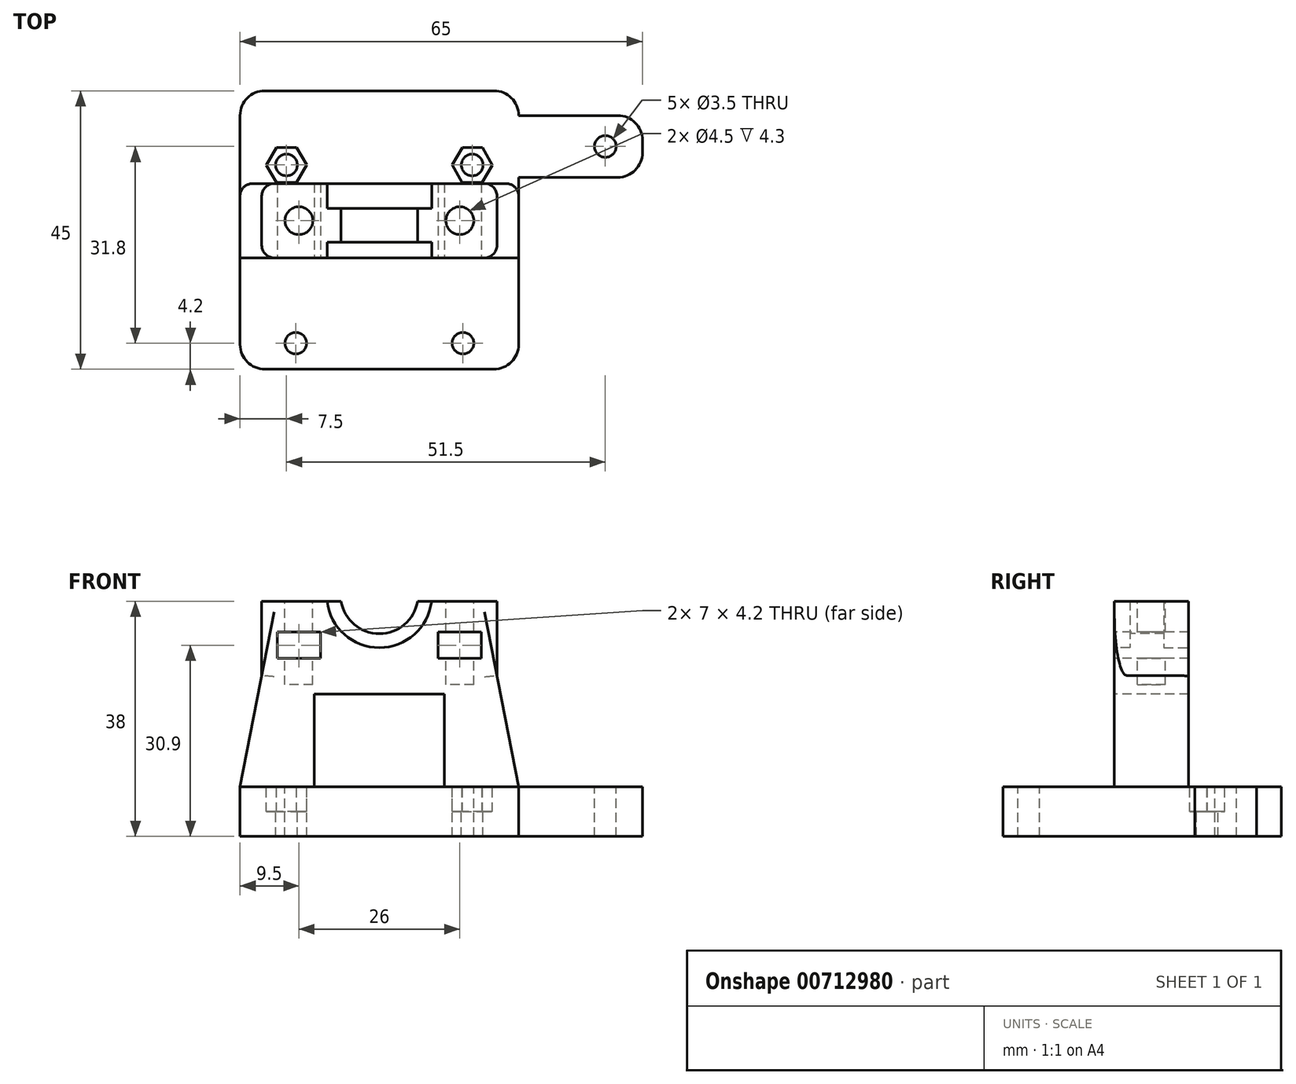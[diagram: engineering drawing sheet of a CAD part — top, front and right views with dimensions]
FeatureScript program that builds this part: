
annotation { "Feature Type Name" : "Feature", "Feature Type Description" : "" }
export const myFeature = defineFeature(function(context is Context, id is Id, definition is map)
    precondition{}
    {
        {
            var Q0;
            Q0=qCreatedBy(makeId("Top.planeOp"),FACE);
            var sketch = newSketch(context, id + "F0", { "sketchPlane" : qUnion([Q0])});
            skLineSegment(sketch, "E0.bottom", {"start": v(22.5, 22.5) * mm, "end": v(-22.5, 22.5) * mm});
            skLineSegment(sketch, "E0.top", {"start": v(22.5, -22.5) * mm, "end": v(-22.5, -22.5) * mm});
            skLineSegment(sketch, "E0.left", {"start": v(22.5, 22.5) * mm, "end": v(22.5, -22.5) * mm});
            skLineSegment(sketch, "E0.right", {"start": v(-22.5, 22.5) * mm, "end": v(-22.5, -22.5) * mm});
            skPoint(sketch, "E0.middle", {"position": v(0, 0) * mm});
            skLineSegment(sketch, "E1.bottom", {"start": v(22.5, 8.5) * mm, "end": v(42.5, 8.5) * mm});
            skLineSegment(sketch, "E1.top", {"start": v(22.5, 18.5) * mm, "end": v(42.5, 18.5) * mm});
            skLineSegment(sketch, "E1.left", {"start": v(22.5, 8.5) * mm, "end": v(22.5, 18.5) * mm});
            skLineSegment(sketch, "E1.right", {"start": v(42.5, 8.5) * mm, "end": v(42.5, 18.5) * mm});
            skSolve(sketch);
        }
        {
            var Q0;
            {var subQ3=sQuery(id+"F0.wireOp",EDGE,"E0.bottom");Q0=makeQuery(id+"F0.imprint","IMPRINT",FACE,{"disambiguationData":[TD([[makeQuery(id+"F0.imprint","IMPRINT",EDGE,{"derivedFrom":subQ3}),1.0]])]});}
            var Q1;
            Q1=makeQuery(id+"F0.imprint","IMPRINT",FACE,{"disambiguationData":[TD([[makeQuery(id+"F0.imprint","IMPRINT",EDGE,{"derivedFrom":sQuery(id+"F0.wireOp",EDGE,"E1.bottom")}),1.0]])]});
            extrude(context, id + "F1", {"entities" : qUnion([Q0, Q1]), "depth" : 8 * mm, "offsetDistance" : 25 * mm});
        }
        {
            var Q0;
            Q0=makeQuery(id+"F1.opExtrude","CAP_FACE",FACE,{"disambiguationData":[OSD([sQuery(id+"F0.wireOp",EDGE,"E0.bottom"),sQuery(id+"F0.wireOp",EDGE,"E0.top"),sQuery(id+"F0.wireOp",EDGE,"E0.left"),sQuery(id+"F0.wireOp",EDGE,"E0.right"),sQuery(id+"F0.wireOp",EDGE,"E1.bottom"),sQuery(id+"F0.wireOp",EDGE,"E1.top"),sQuery(id+"F0.wireOp",EDGE,"E1.right")])],"isStart":false});
            var sketch = newSketch(context, id + "F2", { "sketchPlane" : qUnion([Q0])});
            skLineSegment(sketch, "E2.bottom", {"start": v(-22.5, -4.5) * mm, "end": v(22.5, -4.5) * mm});
            skLineSegment(sketch, "E2.top", {"start": v(-22.5, 7.5) * mm, "end": v(22.5, 7.5) * mm});
            skLineSegment(sketch, "E2.left", {"start": v(-22.5, -4.5) * mm, "end": v(-22.5, 7.5) * mm});
            skLineSegment(sketch, "E2.right", {"start": v(22.5, -4.5) * mm, "end": v(22.5, 7.5) * mm});
            skSolve(sketch);
        }
        {
            var Q0;
            Q0=makeQuery(id+"F2.imprint","IMPRINT",FACE,{"disambiguationData":[TD([[makeQuery(id+"F2.imprint","IMPRINT",EDGE,{"derivedFrom":sQuery(id+"F2.wireOp",EDGE,"E2.bottom")}),1.0]])]});
            extrude(context, id + "F3", {"entities" : qUnion([Q0]), "operationType" : NewBodyOperationType.ADD, "depth" : 18 * mm, "offsetDistance" : 25 * mm});
        }
        {
            var Q0;
            Q0=makeQuery(id+"F3.opExtrude","CAP_FACE",FACE,{"disambiguationData":[OSD([sQuery(id+"F2.wireOp",EDGE,"E2.bottom"),sQuery(id+"F2.wireOp",EDGE,"E2.top"),sQuery(id+"F2.wireOp",EDGE,"E2.left"),sQuery(id+"F2.wireOp",EDGE,"E2.right")])],"isStart":false});
            var sketch = newSketch(context, id + "F4", { "sketchPlane" : qUnion([Q0])});
            skLineSegment(sketch, "E3.bottom", {"start": v(-19, 7.5) * mm, "end": v(19, 7.5) * mm});
            skLineSegment(sketch, "E3.top", {"start": v(-19, -4.5) * mm, "end": v(19, -4.5) * mm});
            skLineSegment(sketch, "E3.left", {"start": v(-19, 7.5) * mm, "end": v(-19, -4.5) * mm});
            skLineSegment(sketch, "E3.right", {"start": v(19, 7.5) * mm, "end": v(19, -4.5) * mm});
            skSolve(sketch);
        }
        {
            var Q0;
            Q0=makeQuery(id+"F4.imprint","IMPRINT",FACE,{"disambiguationData":[TD([[makeQuery(id+"F4.imprint","IMPRINT",EDGE,{"derivedFrom":sQuery(id+"F4.wireOp",EDGE,"E3.bottom")}),-1.0]])]});
            extrude(context, id + "F5", {"entities" : qUnion([Q0]), "operationType" : NewBodyOperationType.ADD, "depth" : 12 * mm, "offsetDistance" : 25 * mm});
        }
        {
            var Q0;
            Q0=makeQuery(id+"F5.boolean.opBoolean","MERGE",FACE,{"derivedFrom":[makeQuery(id+"F3.opExtrude","SWEPT_FACE",FACE,{"disambiguationData":[OSD([sQuery(id+"F2.wireOp",EDGE,"E2.bottom")])]}),makeQuery(id+"F5.opExtrude","SWEPT_FACE",FACE,{"disambiguationData":[OSD([sQuery(id+"F4.wireOp",EDGE,"E3.top")])]})]});
            var sketch = newSketch(context, id + "F6", { "sketchPlane" : qUnion([Q0])});
            skLineSegment(sketch, "E4", {"start": v(-19, 26) * mm, "end": v(-22.5, 8) * mm});
            skLineSegment(sketch, "E5", {"start": v(-22.5, 8) * mm, "end": v(-22.5, 26) * mm});
            skLineSegment(sketch, "E6", {"start": v(-22.5, 26) * mm, "end": v(-19, 26) * mm});
            skLineSegment(sketch, "E7", {"start": v(19, 26) * mm, "end": v(22.5, 26) * mm});
            skLineSegment(sketch, "E8", {"start": v(22.5, 26) * mm, "end": v(22.5, 8) * mm});
            skLineSegment(sketch, "E9", {"start": v(22.5, 8) * mm, "end": v(19, 26) * mm});
            skSolve(sketch);
        }
        {
            var Q0;
            Q0=makeQuery(id+"F6.imprint","IMPRINT",FACE,{"disambiguationData":[TD([[makeQuery(id+"F6.imprint","IMPRINT",EDGE,{"derivedFrom":sQuery(id+"F6.wireOp",EDGE,"E4")}),-1.0]])]});
            var Q1;
            Q1=makeQuery(id+"F6.imprint","IMPRINT",FACE,{"disambiguationData":[TD([[makeQuery(id+"F6.imprint","IMPRINT",EDGE,{"derivedFrom":sQuery(id+"F6.wireOp",EDGE,"E7")}),-1.0]])]});
            extrude(context, id + "F7", {"entities" : qUnion([Q0, Q1]), "operationType" : NewBodyOperationType.REMOVE, "oppositeDirection" : true, "depth" : 25 * mm, "offsetDistance" : 25 * mm});
        }
        {
            var Q0;
            Q0=makeQuery(id+"F5.boolean.opBoolean","MERGE",FACE,{"derivedFrom":[makeQuery(id+"F3.opExtrude","SWEPT_FACE",FACE,{"disambiguationData":[OSD([sQuery(id+"F2.wireOp",EDGE,"E2.bottom")])]}),makeQuery(id+"F5.opExtrude","SWEPT_FACE",FACE,{"disambiguationData":[OSD([sQuery(id+"F4.wireOp",EDGE,"E3.top")])]})]});
            var sketch = newSketch(context, id + "F8", { "sketchPlane" : qUnion([Q0])});
            skLineSegment(sketch, "E10.bottom", {"start": v(-10.5, 8) * mm, "end": v(10.5, 8) * mm});
            skLineSegment(sketch, "E10.top", {"start": v(-10.5, 23) * mm, "end": v(10.5, 23) * mm});
            skLineSegment(sketch, "E10.left", {"start": v(-10.5, 8) * mm, "end": v(-10.5, 23) * mm});
            skLineSegment(sketch, "E10.right", {"start": v(10.5, 8) * mm, "end": v(10.5, 23) * mm});
            skSolve(sketch);
        }
        {
            var Q0;
            Q0=makeQuery(id+"F8.imprint","IMPRINT",FACE,{"disambiguationData":[TD([[makeQuery(id+"F8.imprint","IMPRINT",EDGE,{"derivedFrom":sQuery(id+"F8.wireOp",EDGE,"E10.bottom")}),1.0]])]});
            extrude(context, id + "F9", {"entities" : qUnion([Q0]), "operationType" : NewBodyOperationType.REMOVE, "oppositeDirection" : true, "depth" : 25 * mm, "offsetDistance" : 25 * mm});
        }
        {
            var Q0;
            {var subQ0=sQuery(id+"F0.wireOp",EDGE,"E0.right");var subQ3=sQuery(id+"F0.wireOp",EDGE,"E0.left");var subQ4=sQuery(id+"F0.wireOp",EDGE,"E0.bottom");var subQ6=sQuery(id+"F0.wireOp",EDGE,"E1.top");var subQ7=sQuery(id+"F0.wireOp",EDGE,"E0.top");var subQ8=sQuery(id+"F0.wireOp",EDGE,"E1.bottom");var subQ11=sQuery(id+"F0.wireOp",EDGE,"E1.right");var subQ12=makeQuery(id+"F1.opExtrude","CAP_FACE",FACE,{"disambiguationData":[OSD([subQ4,subQ7,subQ3,subQ0,subQ8,subQ6,subQ11])],"isStart":false});Q0=makeQuery(id+"F9.boolean.opBoolean","MERGE",FACE,{"derivedFrom":[makeQuery(id+"F3.boolean.opBoolean","SPLIT",FACE,{"disambiguationData":[TD([makeQuery(id+"F1.opExtrude","SWEPT_FACE",FACE,{"disambiguationData":[OSD([subQ7])]})])],"derivedFrom":subQ12}),makeQuery(id+"F3.boolean.opBoolean","SPLIT",FACE,{"disambiguationData":[TD([makeQuery(id+"F1.opExtrude","SWEPT_FACE",FACE,{"disambiguationData":[OSD([subQ4])]})])],"derivedFrom":subQ12}),makeQuery(id+"F9.opExtrude","SWEPT_FACE",FACE,{"disambiguationData":[OSD([sQuery(id+"F8.wireOp",EDGE,"E10.bottom")])]})]});}
            var sketch = newSketch(context, id + "F10", { "sketchPlane" : qUnion([Q0])});
            skCircle(sketch, "E11", {"center": v(-15, 10.5) * mm, "radius": 1.75 * mm});
            skLineSegment(sketch, "E12", {"start": v(-15, 10.5) * mm, "end": v(15, 10.5) * mm, "construction": true});
            skCircle(sketch, "E13", {"center": v(15, 10.5) * mm, "radius": 1.75 * mm});
            skSolve(sketch);
        }
        {
            var Q0;
            Q0=makeQuery(id+"F10.imprint","IMPRINT",FACE,{"disambiguationData":[TD([[makeQuery(id+"F10.imprint","IMPRINT",EDGE,{"derivedFrom":sQuery(id+"F10.wireOp",EDGE,"E11")}),1.0]])]});
            var Q1;
            Q1=makeQuery(id+"F10.imprint","IMPRINT",FACE,{"disambiguationData":[TD([[makeQuery(id+"F10.imprint","IMPRINT",EDGE,{"derivedFrom":sQuery(id+"F10.wireOp",EDGE,"E13")}),1.0]])]});
            extrude(context, id + "F11", {"entities" : qUnion([Q0, Q1]), "operationType" : NewBodyOperationType.REMOVE, "oppositeDirection" : true, "depth" : 25 * mm, "offsetDistance" : 25 * mm});
        }
        {
            var Q0;
            {var subQ0=sQuery(id+"F0.wireOp",EDGE,"E0.right");var subQ3=sQuery(id+"F0.wireOp",EDGE,"E0.left");var subQ4=sQuery(id+"F0.wireOp",EDGE,"E0.bottom");var subQ6=sQuery(id+"F0.wireOp",EDGE,"E1.top");var subQ7=sQuery(id+"F0.wireOp",EDGE,"E0.top");var subQ8=sQuery(id+"F0.wireOp",EDGE,"E1.bottom");var subQ11=sQuery(id+"F0.wireOp",EDGE,"E1.right");var subQ12=makeQuery(id+"F1.opExtrude","CAP_FACE",FACE,{"disambiguationData":[OSD([subQ4,subQ7,subQ3,subQ0,subQ8,subQ6,subQ11])],"isStart":false});Q0=makeQuery(id+"F9.boolean.opBoolean","MERGE",FACE,{"derivedFrom":[makeQuery(id+"F3.boolean.opBoolean","SPLIT",FACE,{"disambiguationData":[TD([makeQuery(id+"F1.opExtrude","SWEPT_FACE",FACE,{"disambiguationData":[OSD([subQ7])]})])],"derivedFrom":subQ12}),makeQuery(id+"F3.boolean.opBoolean","SPLIT",FACE,{"disambiguationData":[TD([makeQuery(id+"F1.opExtrude","SWEPT_FACE",FACE,{"disambiguationData":[OSD([subQ4])]})])],"derivedFrom":subQ12}),makeQuery(id+"F9.opExtrude","SWEPT_FACE",FACE,{"disambiguationData":[OSD([sQuery(id+"F8.wireOp",EDGE,"E10.bottom")])]})]});}
            var sketch = newSketch(context, id + "F12", { "sketchPlane" : qUnion([Q0])});
            skCircle(sketch, "E14.cCircle", {"center": v(-15, 10.5) * mm, "radius": 3.25 * mm, "construction": true});
            skLineSegment(sketch, "E14.0", {"start": v(-13.4, 13.32) * mm, "end": v(-11.75, 10.52) * mm});
            skLineSegment(sketch, "E14.1", {"start": v(-11.75, 10.52) * mm, "end": v(-13.36, 7.7) * mm});
            skLineSegment(sketch, "E14.2", {"start": v(-13.36, 7.7) * mm, "end": v(-16.6, 7.68) * mm});
            skLineSegment(sketch, "E14.3", {"start": v(-16.6, 7.68) * mm, "end": v(-18.25, 10.48) * mm});
            skLineSegment(sketch, "E14.4", {"start": v(-18.25, 10.48) * mm, "end": v(-16.64, 13.3) * mm});
            skLineSegment(sketch, "E14.5", {"start": v(-16.64, 13.3) * mm, "end": v(-13.4, 13.32) * mm});
            skCircle(sketch, "E15.cCircle", {"center": v(15, 10.5) * mm, "radius": 3.25 * mm, "construction": true});
            skLineSegment(sketch, "E15.0", {"start": v(18.25, 10.48) * mm, "end": v(16.6, 7.68) * mm});
            skLineSegment(sketch, "E15.1", {"start": v(16.6, 7.68) * mm, "end": v(13.36, 7.7) * mm});
            skLineSegment(sketch, "E15.2", {"start": v(13.36, 7.7) * mm, "end": v(11.75, 10.52) * mm});
            skLineSegment(sketch, "E15.3", {"start": v(11.75, 10.52) * mm, "end": v(13.4, 13.32) * mm});
            skLineSegment(sketch, "E15.4", {"start": v(13.4, 13.32) * mm, "end": v(16.64, 13.3) * mm});
            skLineSegment(sketch, "E15.5", {"start": v(16.64, 13.3) * mm, "end": v(18.25, 10.48) * mm});
            skSolve(sketch);
        }
        {
            var Q0;
            Q0=makeQuery(id+"F12.imprint","IMPRINT",FACE,{"disambiguationData":[TD([[makeQuery(id+"F12.imprint","IMPRINT",EDGE,{"derivedFrom":sQuery(id+"F12.wireOp",EDGE,"E14.0")}),-1.0]])]});
            var Q1;
            Q1=makeQuery(id+"F12.imprint","IMPRINT",FACE,{"disambiguationData":[TD([[makeQuery(id+"F12.imprint","IMPRINT",EDGE,{"derivedFrom":sQuery(id+"F12.wireOp",EDGE,"E15.0")}),-1.0]])]});
            extrude(context, id + "F13", {"entities" : qUnion([Q0, Q1]), "operationType" : NewBodyOperationType.REMOVE, "oppositeDirection" : true, "depth" : 4 * mm, "offsetDistance" : 25 * mm});
        }
        {
            var Q0;
            Q0=makeQuery(id+"F5.boolean.opBoolean","MERGE",FACE,{"derivedFrom":[makeQuery(id+"F3.opExtrude","SWEPT_FACE",FACE,{"disambiguationData":[OSD([sQuery(id+"F2.wireOp",EDGE,"E2.bottom")])]}),makeQuery(id+"F5.opExtrude","SWEPT_FACE",FACE,{"disambiguationData":[OSD([sQuery(id+"F4.wireOp",EDGE,"E3.top")])]})]});
            var sketch = newSketch(context, id + "F14", { "sketchPlane" : qUnion([Q0])});
            skLineSegment(sketch, "E16", {"start": v(0, 38) * mm, "end": v(0, 39) * mm, "construction": true});
            skCircle(sketch, "E17", {"center": v(0, 39) * mm, "radius": 8.5 * mm});
            skCircle(sketch, "E18", {"center": v(0, 39) * mm, "radius": 6.25 * mm});
            skSolve(sketch);
        }
        {
            var Q0;
            Q0 = qSketchRegion(id + "F14", true);
            extrude(context, id + "F15", {"entities" : qUnion([Q0]), "operationType" : NewBodyOperationType.REMOVE, "oppositeDirection" : true, "depth" : 2.5 * mm, "offsetDistance" : 25 * mm});
        }
        {
            var Q0;
            {var subQ0=sQuery(id+"F0.wireOp",EDGE,"E0.right");var subQ3=sQuery(id+"F0.wireOp",EDGE,"E0.left");var subQ4=sQuery(id+"F0.wireOp",EDGE,"E0.bottom");var subQ6=sQuery(id+"F0.wireOp",EDGE,"E1.top");var subQ7=sQuery(id+"F0.wireOp",EDGE,"E0.top");var subQ8=sQuery(id+"F0.wireOp",EDGE,"E1.bottom");var subQ11=sQuery(id+"F0.wireOp",EDGE,"E1.right");var subQ12=makeQuery(id+"F1.opExtrude","CAP_FACE",FACE,{"disambiguationData":[OSD([subQ4,subQ7,subQ3,subQ0,subQ8,subQ6,subQ11])],"isStart":false});Q0=makeQuery(id+"F9.boolean.opBoolean","MERGE",FACE,{"derivedFrom":[makeQuery(id+"F3.boolean.opBoolean","SPLIT",FACE,{"disambiguationData":[TD([makeQuery(id+"F1.opExtrude","SWEPT_FACE",FACE,{"disambiguationData":[OSD([subQ7])]})])],"derivedFrom":subQ12}),makeQuery(id+"F3.boolean.opBoolean","SPLIT",FACE,{"disambiguationData":[TD([makeQuery(id+"F1.opExtrude","SWEPT_FACE",FACE,{"disambiguationData":[OSD([subQ4])]})])],"derivedFrom":subQ12}),makeQuery(id+"F9.opExtrude","SWEPT_FACE",FACE,{"disambiguationData":[OSD([sQuery(id+"F8.wireOp",EDGE,"E10.bottom")])]})]});}
            var sketch = newSketch(context, id + "F16", { "sketchPlane" : qUnion([Q0])});
            skCircle(sketch, "E19", {"center": v(36.5, 13.5) * mm, "radius": 1.75 * mm});
            skPoint(sketch, "E19.centerSnap0", {"position": v(42.5, 13.5) * mm});
            skSolve(sketch);
        }
        {
            var Q0;
            Q0=makeQuery(id+"F16.imprint","IMPRINT",FACE,{"disambiguationData":[TD([[makeQuery(id+"F16.imprint","IMPRINT",EDGE,{"derivedFrom":sQuery(id+"F16.wireOp",EDGE,"E19")}),1.0]])]});
            extrude(context, id + "F17", {"entities" : qUnion([Q0]), "operationType" : NewBodyOperationType.REMOVE, "oppositeDirection" : true, "depth" : 25 * mm, "offsetDistance" : 25 * mm});
        }
        {
            var Q0;
            {var subQ0=sQuery(id+"F4.wireOp",EDGE,"E3.top");var subQ1=sQuery(id+"F4.wireOp",EDGE,"E3.bottom");var subQ2=sQuery(id+"F4.wireOp",EDGE,"E3.left");Q0=makeQuery(id+"FmUpQ3kPXyIInFc_1.boolean.opBoolean","SPLIT",FACE,{"disambiguationData":[TD([makeQuery(id+"F5.opExtrude","SWEPT_FACE",FACE,{"disambiguationData":[OSD([subQ2])]})])],"derivedFrom":makeQuery(id+"F5.opExtrude","CAP_FACE",FACE,{"disambiguationData":[OSD([subQ1,subQ0,subQ2,sQuery(id+"F4.wireOp",EDGE,"E3.right")])],"isStart":false})});}
            var sketch = newSketch(context, id + "F18", { "sketchPlane" : qUnion([Q0])});
            skPoint(sketch, "E20.centerSnap0", {"position": v(0, 7.5) * mm});
            skPoint(sketch, "E20.centerSnap1", {"position": v(-19, 1.5) * mm});
            skCircle(sketch, "E21", {"center": v(13, 1.5) * mm, "radius": 2.25 * mm});
            skCircle(sketch, "E22", {"center": v(-13, 1.5) * mm, "radius": 2.25 * mm});
            skSolve(sketch);
        }
        {
            var Q0;
            Q0=makeQuery(id+"F18.imprint","IMPRINT",FACE,{"disambiguationData":[TD([[makeQuery(id+"F18.imprint","IMPRINT",EDGE,{"derivedFrom":sQuery(id+"F18.wireOp",EDGE,"E20")}),1.0]])]});
            var Q1;
            Q1=makeQuery(id+"F18.imprint","IMPRINT",FACE,{"disambiguationData":[TD([[makeQuery(id+"F18.imprint","IMPRINT",EDGE,{"derivedFrom":sQuery(id+"F18.wireOp",EDGE,"E21")}),1.0]])]});
            var Q2;
            Q2=makeQuery(id+"F18.imprint","IMPRINT",FACE,{"disambiguationData":[TD([[makeQuery(id+"F18.imprint","IMPRINT",EDGE,{"derivedFrom":sQuery(id+"F18.wireOp",EDGE,"E22")}),1.0]])]});
            extrude(context, id + "F19", {"entities" : qUnion([Q0, Q1, Q2]), "operationType" : NewBodyOperationType.REMOVE, "oppositeDirection" : true, "depth" : 13.5 * mm, "offsetDistance" : 25 * mm});
        }
        {
            var Q0;
            Q0=makeQuery(id+"F5.boolean.opBoolean","MERGE",FACE,{"derivedFrom":[makeQuery(id+"F3.opExtrude","SWEPT_FACE",FACE,{"disambiguationData":[OSD([sQuery(id+"F2.wireOp",EDGE,"E2.bottom")])]}),makeQuery(id+"F5.opExtrude","SWEPT_FACE",FACE,{"disambiguationData":[OSD([sQuery(id+"F4.wireOp",EDGE,"E3.top")])]})]});
            var sketch = newSketch(context, id + "F20", { "sketchPlane" : qUnion([Q0])});
            skLineSegment(sketch, "E23.bottom", {"start": v(-16.5, 33) * mm, "end": v(-9.5, 33) * mm});
            skLineSegment(sketch, "E23.top", {"start": v(-16.5, 28.8) * mm, "end": v(-9.5, 28.8) * mm});
            skLineSegment(sketch, "E23.left", {"start": v(-16.5, 33) * mm, "end": v(-16.5, 28.8) * mm});
            skLineSegment(sketch, "E23.right", {"start": v(-9.5, 33) * mm, "end": v(-9.5, 28.8) * mm});
            skLineSegment(sketch, "E24.bottom", {"start": v(16.5, 33) * mm, "end": v(9.5, 33) * mm});
            skLineSegment(sketch, "E24.top", {"start": v(16.5, 28.8) * mm, "end": v(9.5, 28.8) * mm});
            skLineSegment(sketch, "E24.left", {"start": v(16.5, 33) * mm, "end": v(16.5, 28.8) * mm});
            skLineSegment(sketch, "E24.right", {"start": v(9.5, 33) * mm, "end": v(9.5, 28.8) * mm});
            skSolve(sketch);
        }
        {
            var Q0;
            Q0=makeQuery(id+"F20.imprint","IMPRINT",FACE,{"disambiguationData":[TD([[makeQuery(id+"F20.imprint","IMPRINT",EDGE,{"derivedFrom":sQuery(id+"F20.wireOp",EDGE,"E23.bottom")}),-1.0]])]});
            var Q1;
            Q1=makeQuery(id+"F20.imprint","IMPRINT",FACE,{"disambiguationData":[TD([[makeQuery(id+"F20.imprint","IMPRINT",EDGE,{"derivedFrom":sQuery(id+"F20.wireOp",EDGE,"E24.bottom")}),1.0]])]});
            extrude(context, id + "F21", {"entities" : qUnion([Q0, Q1]), "operationType" : NewBodyOperationType.REMOVE, "oppositeDirection" : true, "depth" : 25 * mm, "offsetDistance" : 25 * mm});
        }
        {
            var Q0;
            {var subQ0=sQuery(id+"F0.wireOp",EDGE,"E0.right");var subQ3=sQuery(id+"F0.wireOp",EDGE,"E0.left");var subQ4=sQuery(id+"F0.wireOp",EDGE,"E0.bottom");var subQ6=sQuery(id+"F0.wireOp",EDGE,"E1.top");var subQ7=sQuery(id+"F0.wireOp",EDGE,"E0.top");var subQ8=sQuery(id+"F0.wireOp",EDGE,"E1.bottom");var subQ11=sQuery(id+"F0.wireOp",EDGE,"E1.right");var subQ12=makeQuery(id+"F1.opExtrude","CAP_FACE",FACE,{"disambiguationData":[OSD([subQ4,subQ7,subQ3,subQ0,subQ8,subQ6,subQ11])],"isStart":false});Q0=makeQuery(id+"F9.boolean.opBoolean","MERGE",FACE,{"derivedFrom":[makeQuery(id+"F3.boolean.opBoolean","SPLIT",FACE,{"disambiguationData":[TD([makeQuery(id+"F1.opExtrude","SWEPT_FACE",FACE,{"disambiguationData":[OSD([subQ7])]})])],"derivedFrom":subQ12}),makeQuery(id+"F3.boolean.opBoolean","SPLIT",FACE,{"disambiguationData":[TD([makeQuery(id+"F1.opExtrude","SWEPT_FACE",FACE,{"disambiguationData":[OSD([subQ4])]})])],"derivedFrom":subQ12}),makeQuery(id+"F9.opExtrude","SWEPT_FACE",FACE,{"disambiguationData":[OSD([sQuery(id+"F8.wireOp",EDGE,"E10.bottom")])]})]});}
            var sketch = newSketch(context, id + "F22", { "sketchPlane" : qUnion([Q0])});
            skCircle(sketch, "E25", {"center": v(-13.5, -18.3) * mm, "radius": 1.75 * mm});
            skCircle(sketch, "E26", {"center": v(13.5, -18.3) * mm, "radius": 1.75 * mm});
            skSolve(sketch);
        }
        {
            var Q0;
            Q0=makeQuery(id+"F22.imprint","IMPRINT",FACE,{"disambiguationData":[TD([[makeQuery(id+"F22.imprint","IMPRINT",EDGE,{"derivedFrom":sQuery(id+"F22.wireOp",EDGE,"E25")}),1.0]])]});
            var Q1;
            Q1=makeQuery(id+"F22.imprint","IMPRINT",FACE,{"disambiguationData":[TD([[makeQuery(id+"F22.imprint","IMPRINT",EDGE,{"derivedFrom":sQuery(id+"F22.wireOp",EDGE,"E26")}),1.0]])]});
            extrude(context, id + "F23", {"entities" : qUnion([Q0, Q1]), "operationType" : NewBodyOperationType.REMOVE, "oppositeDirection" : true, "depth" : 25 * mm, "offsetDistance" : 25 * mm});
        }
        {
            var Q0;
            Q0=makeQuery(id+"F1.opExtrude","SWEPT_EDGE",EDGE,{"disambiguationData":[OSD([sQuery(id+"F0.wireOp",EDGE,"E0.top"),sQuery(id+"F0.wireOp",EDGE,"E0.right")])]});
            var Q1;
            Q1=makeQuery(id+"F1.opExtrude","SWEPT_EDGE",EDGE,{"disambiguationData":[OSD([sQuery(id+"F0.wireOp",EDGE,"E0.top"),sQuery(id+"F0.wireOp",EDGE,"E0.left")])]});
            var Q2;
            Q2=makeQuery(id+"F1.opExtrude","SWEPT_EDGE",EDGE,{"disambiguationData":[OSD([sQuery(id+"F0.wireOp",EDGE,"E1.bottom"),sQuery(id+"F0.wireOp",EDGE,"E1.right")])]});
            var Q3;
            Q3=makeQuery(id+"F1.opExtrude","SWEPT_EDGE",EDGE,{"disambiguationData":[OSD([sQuery(id+"F0.wireOp",EDGE,"E1.top"),sQuery(id+"F0.wireOp",EDGE,"E1.right")])]});
            var Q4;
            Q4=makeQuery(id+"F1.opExtrude","SWEPT_EDGE",EDGE,{"disambiguationData":[OSD([sQuery(id+"F0.wireOp",EDGE,"E0.bottom"),sQuery(id+"F0.wireOp",EDGE,"E0.left")])]});
            var Q5;
            Q5=makeQuery(id+"F1.opExtrude","SWEPT_EDGE",EDGE,{"disambiguationData":[OSD([sQuery(id+"F0.wireOp",EDGE,"E0.bottom"),sQuery(id+"F0.wireOp",EDGE,"E0.right")])]});
            fillet(context, id + "F24", {"entities" : qUnion([Q0, Q1, Q2, Q3, Q4, Q5]), "radius" : 4 * mm, "tangentPropagation" : true, "allowEdgeOverflow" : false});
        }
        {
            var Q0;
            Q0=makeQuery(id+"F7.boolean.opBoolean","COPY",EDGE,{"derivedFrom":makeQuery(id+"F7.opExtrude","CAP_EDGE",EDGE,{"disambiguationData":[OSD([sQuery(id+"F6.wireOp",EDGE,"E4")])],"isStart":true})});
            var Q1;
            Q1=makeQuery(id+"F7.boolean.opBoolean","COPY",EDGE,{"derivedFrom":makeQuery(id+"F7.opExtrude","CAP_EDGE",EDGE,{"disambiguationData":[OSD([sQuery(id+"F6.wireOp",EDGE,"E9")])],"isStart":true})});
            var Q2;
            Q2=makeQuery(id+"F7.boolean.opBoolean","INTERSECT",EDGE,{"derivedFrom":[makeQuery(id+"F5.boolean.opBoolean","MERGE",FACE,{"derivedFrom":[makeQuery(id+"F3.opExtrude","SWEPT_FACE",FACE,{"disambiguationData":[OSD([sQuery(id+"F2.wireOp",EDGE,"E2.top")])]}),makeQuery(id+"F5.opExtrude","SWEPT_FACE",FACE,{"disambiguationData":[OSD([sQuery(id+"F4.wireOp",EDGE,"E3.bottom")])]})]}),makeQuery(id+"F7.opExtrude","SWEPT_FACE",FACE,{"disambiguationData":[OSD([sQuery(id+"F6.wireOp",EDGE,"E9")])]})]});
            var Q3;
            Q3=makeQuery(id+"F7.boolean.opBoolean","INTERSECT",EDGE,{"derivedFrom":[makeQuery(id+"F5.boolean.opBoolean","MERGE",FACE,{"derivedFrom":[makeQuery(id+"F3.opExtrude","SWEPT_FACE",FACE,{"disambiguationData":[OSD([sQuery(id+"F2.wireOp",EDGE,"E2.top")])]}),makeQuery(id+"F5.opExtrude","SWEPT_FACE",FACE,{"disambiguationData":[OSD([sQuery(id+"F4.wireOp",EDGE,"E3.bottom")])]})]}),makeQuery(id+"F7.opExtrude","SWEPT_FACE",FACE,{"disambiguationData":[OSD([sQuery(id+"F6.wireOp",EDGE,"E4")])]})]});
            var Q4;
            Q4=makeQuery(id+"F5.opExtrude","SWEPT_EDGE",EDGE,{"disambiguationData":[OSD([sQuery(id+"F2.wireOp",EDGE,"E2.bottom"),sQuery(id+"F4.wireOp",EDGE,"E3.top"),sQuery(id+"F4.wireOp",EDGE,"E3.right")])]});
            var Q5;
            Q5=makeQuery(id+"F5.opExtrude","SWEPT_EDGE",EDGE,{"disambiguationData":[OSD([sQuery(id+"F2.wireOp",EDGE,"E2.top"),sQuery(id+"F4.wireOp",EDGE,"E3.bottom"),sQuery(id+"F4.wireOp",EDGE,"E3.right")])]});
            var Q6;
            Q6=makeQuery(id+"F5.opExtrude","SWEPT_EDGE",EDGE,{"disambiguationData":[OSD([sQuery(id+"F2.wireOp",EDGE,"E2.top"),sQuery(id+"F4.wireOp",EDGE,"E3.bottom"),sQuery(id+"F4.wireOp",EDGE,"E3.left")])]});
            var Q7;
            Q7=makeQuery(id+"F5.opExtrude","SWEPT_EDGE",EDGE,{"disambiguationData":[OSD([sQuery(id+"F2.wireOp",EDGE,"E2.bottom"),sQuery(id+"F4.wireOp",EDGE,"E3.top"),sQuery(id+"F4.wireOp",EDGE,"E3.left")])]});
            fillet(context, id + "F25", {"entities" : qUnion([Q0, Q1, Q2, Q3, Q4, Q5, Q6, Q7]), "radius" : 2 * mm, "tangentPropagation" : true, "allowEdgeOverflow" : false});
        }
        {
            var Q0;
            {var subQ0=sQuery(id+"F4.wireOp",EDGE,"E3.top");Q0=makeQuery(id+"F15.boolean.opBoolean","SPLIT",FACE,{"disambiguationData":[TD([makeQuery(id+"F15.opExtrude","SWEPT_FACE",FACE,{"disambiguationData":[OSD([sQuery(id+"F14.wireOp",EDGE,"E18")])]})])],"derivedFrom":makeQuery(id+"F5.boolean.opBoolean","MERGE",FACE,{"derivedFrom":[makeQuery(id+"F3.opExtrude","SWEPT_FACE",FACE,{"disambiguationData":[OSD([sQuery(id+"F2.wireOp",EDGE,"E2.bottom")])]}),makeQuery(id+"F5.opExtrude","SWEPT_FACE",FACE,{"disambiguationData":[OSD([subQ0])]})]})});}
            extrude(context, id + "F26", {"entities" : qUnion([Q0]), "operationType" : NewBodyOperationType.REMOVE, "oppositeDirection" : true, "depth" : 25 * mm, "offsetDistance" : 25 * mm});
        }
        {
            var Q0;
            Q0=makeQuery(id+"F5.boolean.opBoolean","MERGE",FACE,{"derivedFrom":[makeQuery(id+"F3.opExtrude","SWEPT_FACE",FACE,{"disambiguationData":[OSD([sQuery(id+"F2.wireOp",EDGE,"E2.top")])]}),makeQuery(id+"F5.opExtrude","SWEPT_FACE",FACE,{"disambiguationData":[OSD([sQuery(id+"F4.wireOp",EDGE,"E3.bottom")])]})]});
            var sketch = newSketch(context, id + "F27", { "sketchPlane" : qUnion([Q0])});
            skLineSegment(sketch, "E27", {"start": v(-6.17, 38) * mm, "end": v(6.17, 38) * mm, "construction": true});
            skLineSegment(sketch, "E28", {"start": v(0, 38) * mm, "end": v(0, 39) * mm, "construction": true});
            skCircle(sketch, "E29", {"center": v(0, 39) * mm, "radius": 8.5 * mm});
            skSolve(sketch);
        }
        {
            var Q0;
            {var subQ3=sQuery(id+"F4.wireOp",EDGE,"E3.bottom");var subQ5=sQuery(id+"F2.wireOp",EDGE,"E2.top");var subQ6=makeQuery(id+"F5.opExtrude","SWEPT_FACE",FACE,{"disambiguationData":[OSD([subQ3])]});var subQ7=makeQuery(id+"F3.opExtrude","SWEPT_FACE",FACE,{"disambiguationData":[OSD([subQ5])]});var subQ8=makeQuery(id+"F26.opExtrude","SWEPT_FACE",FACE,{"disambiguationData":[OSD([sQuery(id+"F14.wireOp",EDGE,"E18")])]});var subQ14=makeQuery(id+"F26.boolean.opBoolean","INTERSECT",EDGE,{"derivedFrom":[makeQuery(id+"F5.boolean.opBoolean","MERGE",FACE,{"derivedFrom":[subQ7,subQ6]}),subQ8]});Q0=makeQuery(id+"F27.imprint","IMPRINT",FACE,{"disambiguationData":[TD([[makeQuery(id+"F27.imprint","IMPRINT",EDGE,{"derivedFrom":subQ14}),-1.0]])]});}
            extrude(context, id + "F28", {"entities" : qUnion([Q0]), "operationType" : NewBodyOperationType.REMOVE, "oppositeDirection" : true, "depth" : 4 * mm, "offsetDistance" : 25 * mm});
        }
    });
